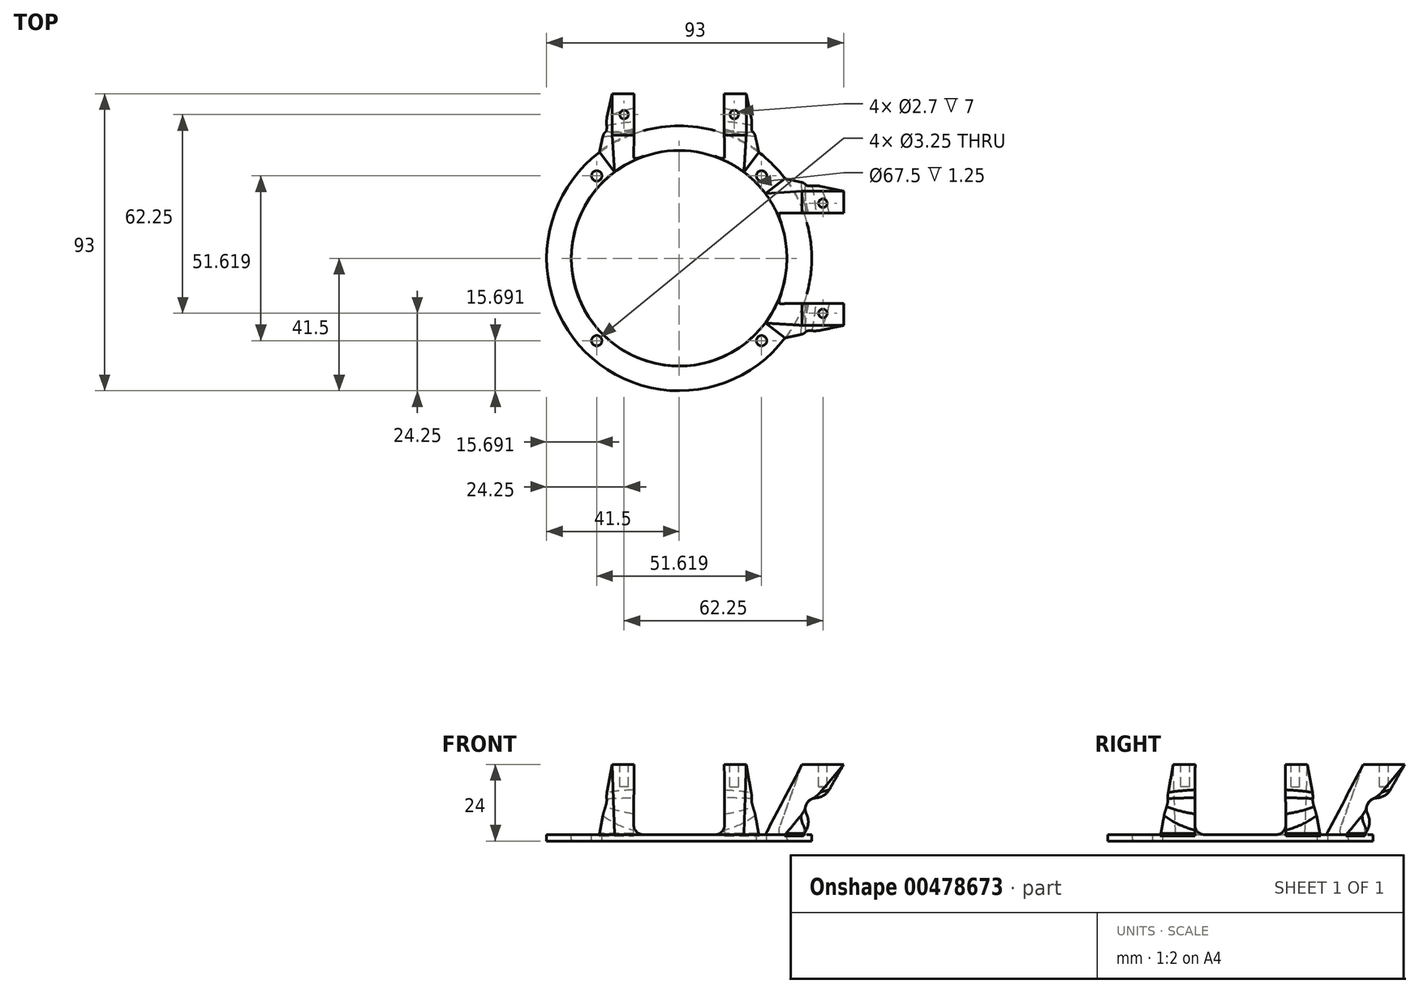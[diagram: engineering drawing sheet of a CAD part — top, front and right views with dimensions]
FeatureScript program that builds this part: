
annotation { "Feature Type Name" : "Feature", "Feature Type Description" : "" }
export const myFeature = defineFeature(function(context is Context, id is Id, definition is map)
    precondition{}
    {
        {
            var Q0;
            Q0=qCreatedBy(makeId("Top.planeOp"),FACE);
            cPlane(context, id + "F0", {"entities" : qUnion([Q0]), "cplaneType" : CPlaneType.OFFSET, "offset" : 22 * mm, "width" : 150 * mm, "height" : 150 * mm});
        }
        {
            var Q0;
            Q0=qCreatedBy(id+"F0.planeOp",FACE);
            var sketch = newSketch(context, id + "F1", { "sketchPlane" : qUnion([Q0])});
            skLineSegment(sketch, "E0.bottom", {"start": v(21, 51.5) * mm, "end": v(14.13, 51.5) * mm});
            skLineSegment(sketch, "E0.top", {"start": v(21, 38.5) * mm, "end": v(14.12, 38.5) * mm});
            skLineSegment(sketch, "E0.left", {"start": v(21, 51.5) * mm, "end": v(21, 38.5) * mm});
            skLineSegment(sketch, "E0.right", {"start": v(-21, 51.5) * mm, "end": v(-21, 38.5) * mm});
            skPoint(sketch, "E0.middle", {"position": v(0, 45) * mm});
            skLineSegment(sketch, "E1", {"start": v(-14.12, 51.5) * mm, "end": v(-14.12, 38.5) * mm});
            skLineSegment(sketch, "E2.MirrorCS", {"start": v(14.12, 51.5) * mm, "end": v(14.12, 38.5) * mm});
            skLineSegment(sketch, "E3.trimOffspring", {"start": v(-14.13, 51.5) * mm, "end": v(-21, 51.5) * mm});
            skLineSegment(sketch, "E4.trimOffspring", {"start": v(-14.13, 38.5) * mm, "end": v(-21, 38.5) * mm});
            skCircle(sketch, "E5", {"center": v(-17.25, 45) * mm, "radius": 1.35 * mm, "construction": true});
            skCircle(sketch, "E6.MirrorC", {"center": v(17.25, 45) * mm, "radius": 1.35 * mm, "construction": true});
            skSolve(sketch);
        }
        {
            var Q0;
            Q0=qCreatedBy(makeId("Top.planeOp"),FACE);
            var sketch = newSketch(context, id + "F2", { "sketchPlane" : qUnion([Q0])});
            skCircle(sketch, "E7", {"center": v(0, 0) * mm, "radius": 40 * mm, "construction": true});
            skCircle(sketch, "E8", {"center": v(0, 0) * mm, "radius": 33.75 * mm});
            skCircle(sketch, "E9", {"center": v(0, 0) * mm, "radius": 36.5 * mm, "construction": true});
            skCircle(sketch, "E10", {"center": v(0, 0) * mm, "radius": 41.5 * mm});
            skCircle(sketch, "E11", {"center": v(-25.8, 25.8) * mm, "radius": 1.63 * mm});
            skLineSegment(sketch, "E12", {"start": v(-25.8, 25.8) * mm, "end": v(0, 0) * mm, "construction": true});
            skCircle(sketch, "E13.1.0", {"center": v(-25.8, -25.8) * mm, "radius": 1.63 * mm});
            skCircle(sketch, "E13.2.0", {"center": v(25.8, -25.8) * mm, "radius": 1.63 * mm});
            skCircle(sketch, "E13.3.0", {"center": v(25.8, 25.8) * mm, "radius": 1.63 * mm});
            skSolve(sketch);
        }
        {
            var Q0;
            Q0=qCreatedBy(makeId("Top.planeOp"),FACE);
            var sketch = newSketch(context, id + "F3", { "sketchPlane" : qUnion([Q0])});
            skCircle(sketch, "E14", {"center": v(0, 0) * mm, "radius": 40 * mm, "construction": true});
            skArc(sketch, "E15", {"start": v(-14.25, 30.6) * mm, "mid": v(0, -33.75) * mm, "end": v(14.25, 30.6) * mm});
            skCircle(sketch, "E16", {"center": v(0, 0) * mm, "radius": 36.5 * mm, "construction": true});
            skArc(sketch, "E17", {"start": v(-14.25, 38.98) * mm, "mid": v(0, -41.5) * mm, "end": v(14.25, 38.98) * mm});
            skCircle(sketch, "E18", {"center": v(-25.8, 25.8) * mm, "radius": 1.63 * mm});
            skLineSegment(sketch, "E19", {"start": v(-25.8, 25.8) * mm, "end": v(0, 0) * mm, "construction": true});
            skCircle(sketch, "E20.1.0", {"center": v(-25.8, -25.8) * mm, "radius": 1.63 * mm});
            skCircle(sketch, "E20.2.0", {"center": v(25.8, -25.8) * mm, "radius": 1.63 * mm});
            skCircle(sketch, "E20.3.0", {"center": v(25.8, 25.8) * mm, "radius": 1.63 * mm});
            skLineSegment(sketch, "E21", {"start": v(-24.93, 33.17) * mm, "end": v(-20.28, 26.98) * mm});
            skLineSegment(sketch, "E22", {"start": v(-14.25, 30.6) * mm, "end": v(-14.25, 38.98) * mm});
            skLineSegment(sketch, "E23.MirrorCS", {"start": v(14.25, 30.6) * mm, "end": v(14.25, 38.98) * mm});
            skLineSegment(sketch, "E24.MirrorCS", {"start": v(24.93, 33.17) * mm, "end": v(20.28, 26.98) * mm});
            skSolve(sketch);
        }
        {
            var Q0;
            {var subQ2=sQuery(id+"F3.wireOp",EDGE,"E21");Q0=makeQuery(id+"F3.imprint","IMPRINT",FACE,{"disambiguationData":[TD([[makeQuery(id+"F3.imprint","IMPRINT",EDGE,{"derivedFrom":subQ2}),1.0]])]});}
            var Q1;
            Q1=makeQuery(id+"F1.imprint","IMPRINT",FACE,{"disambiguationData":[TD([[makeQuery(id+"F1.imprint","IMPRINT",EDGE,{"derivedFrom":sQuery(id+"F1.wireOp",EDGE,"E0.right")}),1.0]])]});
            loft(context, id + "F4", {"sheetProfilesArray" : [{ "sheetProfileEntities" : qUnion([Q0]) }, { "sheetProfileEntities" : qUnion([Q1]) }]});
        }
        {
            var Q0;
            Q0=makeQuery(id+"F4.opLoft","SWEPT_FACE",FACE,{"disambiguationData":[OSD([sQuery(id+"F1.wireOp",EDGE,"E1"),sQuery(id+"F1.wireOp",EDGE,"E3.trimOffspring"),sQuery(id+"F1.wireOp",EDGE,"E4.trimOffspring"),sQuery(id+"F3.wireOp",EDGE,"E15"),sQuery(id+"F3.wireOp",EDGE,"E17"),sQuery(id+"F3.wireOp",EDGE,"E22")])]});
            var sketch = newSketch(context, id + "F5", { "sketchPlane" : qUnion([Q0])});
            skLineSegment(sketch, "E25", {"start": v(45, 21.92) * mm, "end": v(45, 0.92) * mm, "construction": true});
            skLineSegment(sketch, "E26.bottom", {"start": v(47, 11.42) * mm, "end": v(43, 11.42) * mm});
            skLineSegment(sketch, "E26.top", {"start": v(47, 4.42) * mm, "end": v(43, 4.42) * mm});
            skLineSegment(sketch, "E26.left", {"start": v(47, 11.42) * mm, "end": v(47, 4.42) * mm});
            skPoint(sketch, "E26.middle", {"position": v(45, 7.92) * mm});
            skPoint(sketch, "E26.cornerSnap0", {"position": v(45, 11.42) * mm});
            skArc(sketch, "E27", {"start": v(43, 11.42) * mm, "mid": v(39.5, 7.92) * mm, "end": v(43, 4.42) * mm});
            skSolve(sketch);
        }
        {
            var Q0;
            {var subQ0=sQuery(id+"F5.wireOp",EDGE,"E27");var subQ1=sQuery(id+"F5.wireOp",EDGE,"E26.bottom");var subQ2=makeQuery(id+"F5.imprint","INTERSECT",VERTEX,{"derivedFrom":[subQ1,subQ0]});Q0=makeQuery(id+"F5.imprint","IMPRINT",FACE,{"disambiguationData":[TD([[makeQuery(id+"F5.imprint","IMPRINT",EDGE,{"disambiguationData":[TD([[subQ2,1.0]])],"derivedFrom":subQ1}),1.0]])]});}
            extrude(context, id + "F6", {"entities" : qUnion([Q0]), "operationType" : NewBodyOperationType.REMOVE, "oppositeDirection" : true, "depth" : 25 * mm});
        }
        {
            var Q0;
            Q0=makeQuery(id+"F6.boolean.opBoolean","INTERSECT",EDGE,{"disambiguationData":[OD(0.0)],"derivedFrom":[makeQuery(id+"F4.opLoft","SWEPT_FACE",FACE,{"disambiguationData":[OSD([sQuery(id+"F1.wireOp",EDGE,"E0.right"),sQuery(id+"F1.wireOp",EDGE,"E1"),sQuery(id+"F1.wireOp",EDGE,"E3.trimOffspring"),sQuery(id+"F3.wireOp",EDGE,"E17"),sQuery(id+"F3.wireOp",EDGE,"E21"),sQuery(id+"F3.wireOp",EDGE,"E22")])]}),makeQuery(id+"F6.opExtrude","SWEPT_FACE",FACE,{"disambiguationData":[OSD([sQuery(id+"F5.wireOp",EDGE,"E27")])]})]});
            var Q1;
            Q1=makeQuery(id+"F6.boolean.opBoolean","INTERSECT",EDGE,{"derivedFrom":[makeQuery(id+"F4.opLoft","SWEPT_FACE",FACE,{"disambiguationData":[OSD([sQuery(id+"F1.wireOp",EDGE,"E0.right"),sQuery(id+"F1.wireOp",EDGE,"E1"),sQuery(id+"F1.wireOp",EDGE,"E3.trimOffspring"),sQuery(id+"F3.wireOp",EDGE,"E17"),sQuery(id+"F3.wireOp",EDGE,"E21"),sQuery(id+"F3.wireOp",EDGE,"E22")])]}),makeQuery(id+"F6.opExtrude","SWEPT_FACE",FACE,{"disambiguationData":[OSD([sQuery(id+"F5.wireOp",EDGE,"E26.bottom")])]})]});
            var Q2;
            Q2=makeQuery(id+"F6.boolean.opBoolean","INTERSECT",EDGE,{"disambiguationData":[OD(1.0)],"derivedFrom":[makeQuery(id+"F4.opLoft","SWEPT_FACE",FACE,{"disambiguationData":[OSD([sQuery(id+"F1.wireOp",EDGE,"E0.right"),sQuery(id+"F1.wireOp",EDGE,"E1"),sQuery(id+"F1.wireOp",EDGE,"E3.trimOffspring"),sQuery(id+"F3.wireOp",EDGE,"E17"),sQuery(id+"F3.wireOp",EDGE,"E21"),sQuery(id+"F3.wireOp",EDGE,"E22")])]}),makeQuery(id+"F6.opExtrude","SWEPT_FACE",FACE,{"disambiguationData":[OSD([sQuery(id+"F5.wireOp",EDGE,"E27")])]})]});
            fillet(context, id + "F7", {"entities" : qUnion([Q0, Q1, Q2]), "radius" : 5 * mm, "tangentPropagation" : true, "allowEdgeOverflow" : false});
        }
        {
            var Q0;
            Q0=makeQuery(id+"F2.imprint","IMPRINT",FACE,{"disambiguationData":[TD([[makeQuery(id+"F2.imprint","IMPRINT",EDGE,{"derivedFrom":sQuery(id+"F2.wireOp",EDGE,"E8")}),-1.0]])]});
            extrude(context, id + "F8", {"entities" : qUnion([Q0]), "oppositeDirection" : true, "depth" : 2 * mm});
        }
        {
            var Q0;
            Q0=makeQuery(id+"F4.opLoft","CAP_FACE",FACE,{"disambiguationData":[OSD([makeQuery(id+"F1.imprint","IMPRINT",FACE,{"disambiguationData":[TD([[makeQuery(id+"F1.imprint","IMPRINT",EDGE,{"derivedFrom":sQuery(id+"F1.wireOp",EDGE,"E0.right")}),1.0]])]})])],"isStart":true});
            var sketch = newSketch(context, id + "F9", { "sketchPlane" : qUnion([Q0])});
            skCircle(sketch, "E28", {"center": v(-17.25, 45) * mm, "radius": 1.35 * mm});
            skPoint(sketch, "E28.centerSnap0", {"position": v(-14.12, 45) * mm});
            skSolve(sketch);
        }
        {
            var Q0;
            Q0=makeQuery(id+"F9.imprint","IMPRINT",FACE,{"disambiguationData":[TD([[makeQuery(id+"F9.imprint","IMPRINT",EDGE,{"derivedFrom":sQuery(id+"F9.wireOp",EDGE,"E28")}),1.0]])]});
            extrude(context, id + "F10", {"entities" : qUnion([Q0]), "operationType" : NewBodyOperationType.REMOVE, "oppositeDirection" : true, "depth" : 7 * mm});
        }
        {
            var Q0;
            {var subQ2=sQuery(id+"F3.wireOp",EDGE,"E21");Q0=makeQuery(id+"F4.opLoft","SWEPT_BODY",BODY,{"disambiguationData":[OSD([makeQuery(id+"F1.imprint","IMPRINT",FACE,{"disambiguationData":[TD([[makeQuery(id+"F1.imprint","IMPRINT",EDGE,{"derivedFrom":sQuery(id+"F1.wireOp",EDGE,"E0.right")}),1.0]])]}),makeQuery(id+"F3.imprint","IMPRINT",FACE,{"disambiguationData":[TD([[makeQuery(id+"F3.imprint","IMPRINT",EDGE,{"derivedFrom":subQ2}),1.0]])]})])]});}
            var Q1;
            Q1=qCreatedBy(makeId("Right.planeOp"),FACE);
            mirror(context, id + "F11", {"entities" : qUnion([Q0]), "mirrorPlane" : qUnion([Q1])});
        }
        {
            var Q0;
            {var subQ2=sQuery(id+"F3.wireOp",EDGE,"E21");Q0=makeQuery(id+"F4.opLoft","SWEPT_BODY",BODY,{"disambiguationData":[OSD([makeQuery(id+"F1.imprint","IMPRINT",FACE,{"disambiguationData":[TD([[makeQuery(id+"F1.imprint","IMPRINT",EDGE,{"derivedFrom":sQuery(id+"F1.wireOp",EDGE,"E0.right")}),1.0]])]}),makeQuery(id+"F3.imprint","IMPRINT",FACE,{"disambiguationData":[TD([[makeQuery(id+"F3.imprint","IMPRINT",EDGE,{"derivedFrom":subQ2}),1.0]])]})])]});}
            var Q1;
            {var subQ2=sQuery(id+"F3.wireOp",EDGE,"E21");Q1=makeQuery(id+"F11.opPattern","COPY",BODY,{"derivedFrom":makeQuery(id+"F4.opLoft","SWEPT_BODY",BODY,{"disambiguationData":[OSD([makeQuery(id+"F1.imprint","IMPRINT",FACE,{"disambiguationData":[TD([[makeQuery(id+"F1.imprint","IMPRINT",EDGE,{"derivedFrom":sQuery(id+"F1.wireOp",EDGE,"E0.right")}),1.0]])]}),makeQuery(id+"F3.imprint","IMPRINT",FACE,{"disambiguationData":[TD([[makeQuery(id+"F3.imprint","IMPRINT",EDGE,{"derivedFrom":subQ2}),1.0]])]})])]}),"instanceName":"1"});}
            var Q2;
            Q2=sQuery(id+"F2.wireOp",EDGE,"E8");
            circularPattern(context, id + "F12", {"entities" : qUnion([Q0, Q1]), "axis" : qUnion([Q2]), "angle" : 270 * degree, "instanceCount" : 2, "equalSpace" : true});
        }
        {
            var Q0;
            {var subQ2=sQuery(id+"F3.wireOp",EDGE,"E21");Q0=makeQuery(id+"F4.opLoft","SWEPT_BODY",BODY,{"disambiguationData":[OSD([makeQuery(id+"F1.imprint","IMPRINT",FACE,{"disambiguationData":[TD([[makeQuery(id+"F1.imprint","IMPRINT",EDGE,{"derivedFrom":sQuery(id+"F1.wireOp",EDGE,"E0.right")}),1.0]])]}),makeQuery(id+"F3.imprint","IMPRINT",FACE,{"disambiguationData":[TD([[makeQuery(id+"F3.imprint","IMPRINT",EDGE,{"derivedFrom":subQ2}),1.0]])]})])]});}
            var Q1;
            Q1=makeQuery(id+"F8.opExtrude","SWEPT_BODY",BODY,{"disambiguationData":[OSD([sQuery(id+"F2.wireOp",EDGE,"E8"),sQuery(id+"F2.wireOp",EDGE,"E10"),sQuery(id+"F2.wireOp",EDGE,"E11"),sQuery(id+"F2.wireOp",EDGE,"E13.1.0"),sQuery(id+"F2.wireOp",EDGE,"E13.2.0"),sQuery(id+"F2.wireOp",EDGE,"E13.3.0")])]});
            var Q2;
            {var subQ2=sQuery(id+"F3.wireOp",EDGE,"E21");Q2=makeQuery(id+"F11.opPattern","COPY",BODY,{"derivedFrom":makeQuery(id+"F4.opLoft","SWEPT_BODY",BODY,{"disambiguationData":[OSD([makeQuery(id+"F1.imprint","IMPRINT",FACE,{"disambiguationData":[TD([[makeQuery(id+"F1.imprint","IMPRINT",EDGE,{"derivedFrom":sQuery(id+"F1.wireOp",EDGE,"E0.right")}),1.0]])]}),makeQuery(id+"F3.imprint","IMPRINT",FACE,{"disambiguationData":[TD([[makeQuery(id+"F3.imprint","IMPRINT",EDGE,{"derivedFrom":subQ2}),1.0]])]})])]}),"instanceName":"1"});}
            var Q3;
            {var subQ2=sQuery(id+"F3.wireOp",EDGE,"E21");Q3=makeQuery(id+"F12.opPattern","COPY",BODY,{"derivedFrom":makeQuery(id+"F4.opLoft","SWEPT_BODY",BODY,{"disambiguationData":[OSD([makeQuery(id+"F1.imprint","IMPRINT",FACE,{"disambiguationData":[TD([[makeQuery(id+"F1.imprint","IMPRINT",EDGE,{"derivedFrom":sQuery(id+"F1.wireOp",EDGE,"E0.right")}),1.0]])]}),makeQuery(id+"F3.imprint","IMPRINT",FACE,{"disambiguationData":[TD([[makeQuery(id+"F3.imprint","IMPRINT",EDGE,{"derivedFrom":subQ2}),1.0]])]})])]}),"instanceName":"1"});}
            var Q4;
            {var subQ2=sQuery(id+"F3.wireOp",EDGE,"E21");Q4=makeQuery(id+"F12.opPattern","COPY",BODY,{"derivedFrom":makeQuery(id+"F11.opPattern","COPY",BODY,{"derivedFrom":makeQuery(id+"F4.opLoft","SWEPT_BODY",BODY,{"disambiguationData":[OSD([makeQuery(id+"F1.imprint","IMPRINT",FACE,{"disambiguationData":[TD([[makeQuery(id+"F1.imprint","IMPRINT",EDGE,{"derivedFrom":sQuery(id+"F1.wireOp",EDGE,"E0.right")}),1.0]])]}),makeQuery(id+"F3.imprint","IMPRINT",FACE,{"disambiguationData":[TD([[makeQuery(id+"F3.imprint","IMPRINT",EDGE,{"derivedFrom":subQ2}),1.0]])]})])]}),"instanceName":"1"}),"instanceName":"1"});}
            booleanBodies(context, id + "F13", {"operationType" : BooleanOperationType.UNION, "tools" : qUnion([Q0, Q1, Q2, Q3, Q4])});
        }
        {
            var Q0;
            Q0=makeQuery(id+"F4.opLoft","MID_CAP_EDGE",EDGE,{"disambiguationData":[OSD([sQuery(id+"F3.wireOp",EDGE,"E15"),sQuery(id+"F3.wireOp",EDGE,"E17"),sQuery(id+"F3.wireOp",EDGE,"E22")])],"capPos":0.0});
            var Q1;
            Q1=makeQuery(id+"F11.opPattern","COPY",EDGE,{"derivedFrom":makeQuery(id+"F4.opLoft","MID_CAP_EDGE",EDGE,{"disambiguationData":[OSD([sQuery(id+"F3.wireOp",EDGE,"E15"),sQuery(id+"F3.wireOp",EDGE,"E17"),sQuery(id+"F3.wireOp",EDGE,"E22")])],"capPos":0.0}),"instanceName":"1"});
            var Q2;
            Q2=makeQuery(id+"F12.opPattern","COPY",EDGE,{"derivedFrom":makeQuery(id+"F4.opLoft","MID_CAP_EDGE",EDGE,{"disambiguationData":[OSD([sQuery(id+"F3.wireOp",EDGE,"E15"),sQuery(id+"F3.wireOp",EDGE,"E17"),sQuery(id+"F3.wireOp",EDGE,"E22")])],"capPos":0.0}),"instanceName":"1"});
            var Q3;
            Q3=makeQuery(id+"F12.opPattern","COPY",EDGE,{"derivedFrom":makeQuery(id+"F11.opPattern","COPY",EDGE,{"derivedFrom":makeQuery(id+"F4.opLoft","MID_CAP_EDGE",EDGE,{"disambiguationData":[OSD([sQuery(id+"F3.wireOp",EDGE,"E15"),sQuery(id+"F3.wireOp",EDGE,"E17"),sQuery(id+"F3.wireOp",EDGE,"E22")])],"capPos":0.0}),"instanceName":"1"}),"instanceName":"1"});
            fillet(context, id + "F14", {"entities" : qUnion([Q0, Q1, Q2, Q3]), "radius" : 3 * mm, "tangentPropagation" : true, "allowEdgeOverflow" : false});
        }
        {
            var Q0;
            Q0=makeQuery(id+"F8.opExtrude","CAP_EDGE",EDGE,{"disambiguationData":[OSD([sQuery(id+"F2.wireOp",EDGE,"E8")])],"isStart":false});
            fillet(context, id + "F15", {"entities" : qUnion([Q0]), "radius" : 0.75 * mm, "tangentPropagation" : true, "allowEdgeOverflow" : false});
        }
        {
            var Q0;
            Q0=makeQuery(id+"F13.opBoolean","MERGE",EDGE,{"derivedFrom":[makeQuery(id+"F8.opExtrude","CAP_EDGE",EDGE,{"disambiguationData":[OSD([sQuery(id+"F2.wireOp",EDGE,"E10")])],"isStart":true}),makeQuery(id+"F11.opPattern","COPY",EDGE,{"derivedFrom":makeQuery(id+"F4.opLoft","MID_CAP_EDGE",EDGE,{"disambiguationData":[OSD([sQuery(id+"F3.wireOp",EDGE,"E17"),sQuery(id+"F3.wireOp",EDGE,"E21"),sQuery(id+"F3.wireOp",EDGE,"E22")])],"capPos":0.0}),"instanceName":"1"})]});
            var Q1;
            Q1=makeQuery(id+"F13.opBoolean","MERGE",EDGE,{"derivedFrom":[makeQuery(id+"F8.opExtrude","CAP_EDGE",EDGE,{"disambiguationData":[OSD([sQuery(id+"F2.wireOp",EDGE,"E10")])],"isStart":true}),makeQuery(id+"F12.opPattern","COPY",EDGE,{"derivedFrom":makeQuery(id+"F4.opLoft","MID_CAP_EDGE",EDGE,{"disambiguationData":[OSD([sQuery(id+"F3.wireOp",EDGE,"E17"),sQuery(id+"F3.wireOp",EDGE,"E21"),sQuery(id+"F3.wireOp",EDGE,"E22")])],"capPos":0.0}),"instanceName":"1"})]});
            var Q2;
            Q2=makeQuery(id+"F13.opBoolean","MERGE",EDGE,{"derivedFrom":[makeQuery(id+"F8.opExtrude","CAP_EDGE",EDGE,{"disambiguationData":[OSD([sQuery(id+"F2.wireOp",EDGE,"E10")])],"isStart":true}),makeQuery(id+"F12.opPattern","COPY",EDGE,{"derivedFrom":makeQuery(id+"F11.opPattern","COPY",EDGE,{"derivedFrom":makeQuery(id+"F4.opLoft","MID_CAP_EDGE",EDGE,{"disambiguationData":[OSD([sQuery(id+"F3.wireOp",EDGE,"E17"),sQuery(id+"F3.wireOp",EDGE,"E21"),sQuery(id+"F3.wireOp",EDGE,"E22")])],"capPos":0.0}),"instanceName":"1"}),"instanceName":"1"})]});
            var Q3;
            Q3=makeQuery(id+"F13.opBoolean","MERGE",EDGE,{"derivedFrom":[makeQuery(id+"F4.opLoft","MID_CAP_EDGE",EDGE,{"disambiguationData":[OSD([sQuery(id+"F3.wireOp",EDGE,"E17"),sQuery(id+"F3.wireOp",EDGE,"E21"),sQuery(id+"F3.wireOp",EDGE,"E22")])],"capPos":0.0}),makeQuery(id+"F8.opExtrude","CAP_EDGE",EDGE,{"disambiguationData":[OSD([sQuery(id+"F2.wireOp",EDGE,"E10")])],"isStart":true})]});
            chamfer(context, id + "F16", {"entities" : qUnion([Q0, Q1, Q2, Q3]), "width" : 1.5 * mm, "tangentPropagation" : true});
        }
    });
